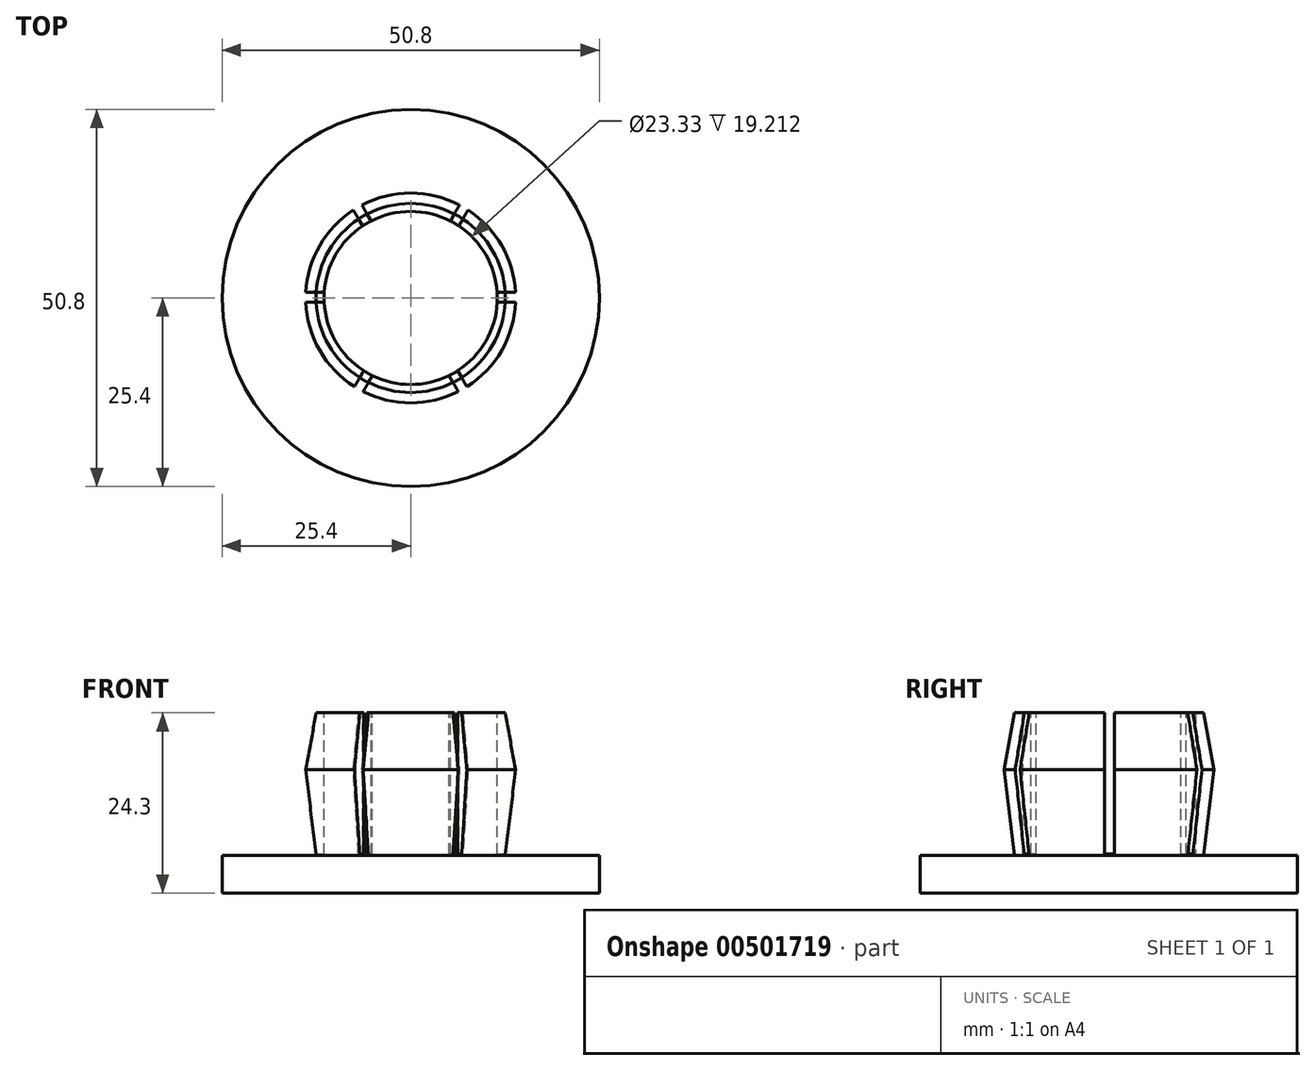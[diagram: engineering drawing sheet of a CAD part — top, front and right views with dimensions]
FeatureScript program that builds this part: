
annotation { "Feature Type Name" : "Feature", "Feature Type Description" : "" }
export const myFeature = defineFeature(function(context is Context, id is Id, definition is map)
    precondition{}
    {
        {
            var Q0;
            Q0=qCreatedBy(makeId("Top.planeOp"),FACE);
            var sketch = newSketch(context, id + "F0", { "sketchPlane" : qUnion([Q0])});
            skCircle(sketch, "E0", {"center": v(0, 0) * mm, "radius": 13.34 * mm});
            skCircle(sketch, "E1", {"center": v(0, 0) * mm, "radius": 25.4 * mm});
            skSolve(sketch);
        }
        {
            var Q0;
            Q0=makeQuery(id+"F0.imprint","IMPRINT",FACE,{"disambiguationData":[TD([[makeQuery(id+"F0.imprint","IMPRINT",EDGE,{"derivedFrom":sQuery(id+"F0.wireOp",EDGE,"E0")}),-1.0]])]});
            var Q1;
            Q1=makeQuery(id+"F0.imprint","IMPRINT",FACE,{"disambiguationData":[TD([[makeQuery(id+"F0.imprint","IMPRINT",EDGE,{"derivedFrom":sQuery(id+"F0.wireOp",EDGE,"E0")}),1.0]])]});
            extrude(context, id + "F1", {"entities" : qUnion([Q0, Q1]), "depth" : 5.08 * mm});
        }
        {
            var Q0;
            Q0=makeQuery(id+"F1.opExtrude","CAP_FACE",FACE,{"disambiguationData":[OSD([sQuery(id+"F0.wireOp",EDGE,"E1")])],"isStart":false});
            var sketch = newSketch(context, id + "F2", { "sketchPlane" : qUnion([Q0])});
            skCircle(sketch, "E2", {"center": v(0, 0) * mm, "radius": 13.34 * mm});
            skCircle(sketch, "E3", {"center": v(0, 0) * mm, "radius": 11.67 * mm});
            skSolve(sketch);
        }
        {
            var Q0;
            Q0=qCreatedBy(makeId("Right.planeOp"),FACE);
            var sketch = newSketch(context, id + "F3", { "sketchPlane" : qUnion([Q0])});
            skLineSegment(sketch, "E4", {"start": v(0, 5.08) * mm, "end": v(-12.74, 5.08) * mm});
            skLineSegment(sketch, "E5", {"start": v(-12.74, 5.08) * mm, "end": v(-14.14, 16.63) * mm});
            skLineSegment(sketch, "E6", {"start": v(-14.14, 16.63) * mm, "end": v(-12.74, 24.3) * mm});
            skLineSegment(sketch, "E7", {"start": v(-12.74, 24.3) * mm, "end": v(0, 24.3) * mm});
            skLineSegment(sketch, "E8", {"start": v(0, 24.3) * mm, "end": v(0, 5.08) * mm});
            skSolve(sketch);
        }
        {
            var Q0;
            Q0=makeQuery(id+"F3.imprint","IMPRINT",FACE,{"disambiguationData":[TD([[makeQuery(id+"F3.imprint","IMPRINT",EDGE,{"derivedFrom":sQuery(id+"F3.wireOp",EDGE,"E4")}),-1.0]])]});
            var Q1;
            Q1=sQuery(id+"F3.wireOp",EDGE,"E8");
            revolve(context, id + "F4", {"operationType" : NewBodyOperationType.ADD, "entities" : qUnion([Q0]), "axis" : qUnion([Q1]), "revolveType" : RevolveType.FULL});
        }
        {
            var Q0;
            Q0=makeQuery(id+"F2.imprint","IMPRINT",FACE,{"disambiguationData":[TD([[makeQuery(id+"F2.imprint","IMPRINT",EDGE,{"derivedFrom":sQuery(id+"F2.wireOp",EDGE,"E3")}),1.0]])]});
            extrude(context, id + "F5", {"entities" : qUnion([Q0]), "operationType" : NewBodyOperationType.REMOVE, "depth" : 25.4 * mm});
        }
        {
            var Q0;
            Q0=makeQuery(id+"F4.opRevolve","SWEPT_FACE",FACE,{"disambiguationData":[OSD([sQuery(id+"F3.wireOp",EDGE,"E7")])]});
            var sketch = newSketch(context, id + "F6", { "sketchPlane" : qUnion([Q0])});
            skLineSegment(sketch, "E9.bottom", {"start": v(-15.03, 0.76) * mm, "end": v(14.96, 0.76) * mm});
            skLineSegment(sketch, "E9.top", {"start": v(-15.03, -0.57) * mm, "end": v(14.96, -0.57) * mm});
            skLineSegment(sketch, "E9.left", {"start": v(-15.03, 0.76) * mm, "end": v(-15.03, -0.57) * mm});
            skLineSegment(sketch, "E9.right", {"start": v(14.96, 0.76) * mm, "end": v(14.96, -0.57) * mm});
            skLineSegment(sketch, "E10.1.0", {"start": v(6.85, -13.4) * mm, "end": v(8.01, -12.73) * mm});
            skLineSegment(sketch, "E10.1.1", {"start": v(6.85, -13.4) * mm, "end": v(-8.14, 12.57) * mm});
            skLineSegment(sketch, "E10.1.2", {"start": v(8.01, -12.73) * mm, "end": v(-6.98, 13.24) * mm});
            skLineSegment(sketch, "E10.1.3", {"start": v(-8.14, 12.57) * mm, "end": v(-6.98, 13.24) * mm});
            skLineSegment(sketch, "E10.2.0", {"start": v(8.18, 12.63) * mm, "end": v(7.02, 13.3) * mm});
            skLineSegment(sketch, "E10.2.1", {"start": v(8.18, 12.63) * mm, "end": v(-6.82, -13.34) * mm});
            skLineSegment(sketch, "E10.2.2", {"start": v(7.02, 13.3) * mm, "end": v(-7.98, -12.67) * mm});
            skLineSegment(sketch, "E10.2.3", {"start": v(-6.82, -13.34) * mm, "end": v(-7.98, -12.67) * mm});
            skPoint(sketch, "E10.center", {"position": v(0, 0) * mm});
            skSolve(sketch);
        }
        {
            var Q0;
            {var subQ0=sQuery(id+"F6.wireOp",EDGE,"E9.left");Q0=makeQuery(id+"F6.imprint","IMPRINT",FACE,{"disambiguationData":[TD([[makeQuery(id+"F6.imprint","IMPRINT",EDGE,{"derivedFrom":subQ0}),1.0]])]});}
            var Q1;
            {var subQ0=sQuery(id+"F6.wireOp",EDGE,"E9.bottom");var subQ1=sQuery(id+"F3.wireOp",EDGE,"E7");var subQ2=makeQuery(id+"F4.opRevolve","SWEPT_EDGE",EDGE,{"disambiguationData":[OSD([sQuery(id+"F3.wireOp",EDGE,"E6"),subQ1])]});var subQ3=makeQuery(id+"F6.imprint","INTERSECT",VERTEX,{"disambiguationData":[OD(0.0)],"derivedFrom":[subQ2,subQ0]});Q1=makeQuery(id+"F6.imprint","IMPRINT",FACE,{"disambiguationData":[TD([[makeQuery(id+"F6.imprint","IMPRINT",EDGE,{"disambiguationData":[TD([[subQ3,-1.0]])],"derivedFrom":subQ0}),-1.0]])]});}
            var Q2;
            {var subQ0=sQuery(id+"F6.wireOp",EDGE,"E10.1.3");Q2=makeQuery(id+"F6.imprint","IMPRINT",FACE,{"disambiguationData":[TD([[makeQuery(id+"F6.imprint","IMPRINT",EDGE,{"derivedFrom":subQ0}),-1.0]])]});}
            var Q3;
            {var subQ0=sQuery(id+"F6.wireOp",EDGE,"E10.1.1");var subQ1=sQuery(id+"F3.wireOp",EDGE,"E7");var subQ2=makeQuery(id+"F4.opRevolve","SWEPT_EDGE",EDGE,{"disambiguationData":[OSD([sQuery(id+"F3.wireOp",EDGE,"E6"),subQ1])]});var subQ3=makeQuery(id+"F6.imprint","INTERSECT",VERTEX,{"disambiguationData":[OD(1.0)],"derivedFrom":[subQ2,subQ0]});Q3=makeQuery(id+"F6.imprint","IMPRINT",FACE,{"disambiguationData":[TD([[makeQuery(id+"F6.imprint","IMPRINT",EDGE,{"disambiguationData":[TD([[subQ3,1.0]])],"derivedFrom":subQ0}),-1.0]])]});}
            var Q4;
            {var subQ0=sQuery(id+"F6.wireOp",EDGE,"E10.2.0");Q4=makeQuery(id+"F6.imprint","IMPRINT",FACE,{"disambiguationData":[TD([[makeQuery(id+"F6.imprint","IMPRINT",EDGE,{"derivedFrom":subQ0}),1.0]])]});}
            var Q5;
            {var subQ0=sQuery(id+"F6.wireOp",EDGE,"E10.2.1");var subQ1=sQuery(id+"F3.wireOp",EDGE,"E7");var subQ2=makeQuery(id+"F4.opRevolve","SWEPT_EDGE",EDGE,{"disambiguationData":[OSD([sQuery(id+"F3.wireOp",EDGE,"E6"),subQ1])]});var subQ3=makeQuery(id+"F6.imprint","INTERSECT",VERTEX,{"disambiguationData":[OD(0.0)],"derivedFrom":[subQ2,subQ0]});Q5=makeQuery(id+"F6.imprint","IMPRINT",FACE,{"disambiguationData":[TD([[makeQuery(id+"F6.imprint","IMPRINT",EDGE,{"disambiguationData":[TD([[subQ3,-1.0]])],"derivedFrom":subQ0}),-1.0]])]});}
            var Q6;
            {var subQ0=sQuery(id+"F6.wireOp",EDGE,"E9.bottom");var subQ1=sQuery(id+"F3.wireOp",EDGE,"E7");var subQ2=makeQuery(id+"F4.opRevolve","SWEPT_EDGE",EDGE,{"disambiguationData":[OSD([sQuery(id+"F3.wireOp",EDGE,"E6"),subQ1])]});var subQ3=makeQuery(id+"F6.imprint","INTERSECT",VERTEX,{"disambiguationData":[OD(1.0)],"derivedFrom":[subQ2,subQ0]});Q6=makeQuery(id+"F6.imprint","IMPRINT",FACE,{"disambiguationData":[TD([[makeQuery(id+"F6.imprint","IMPRINT",EDGE,{"disambiguationData":[TD([[subQ3,1.0]])],"derivedFrom":subQ0}),-1.0]])]});}
            var Q7;
            {var subQ0=sQuery(id+"F6.wireOp",EDGE,"E9.right");Q7=makeQuery(id+"F6.imprint","IMPRINT",FACE,{"disambiguationData":[TD([[makeQuery(id+"F6.imprint","IMPRINT",EDGE,{"derivedFrom":subQ0}),-1.0]])]});}
            var Q8;
            {var subQ0=sQuery(id+"F6.wireOp",EDGE,"E10.1.1");var subQ1=sQuery(id+"F3.wireOp",EDGE,"E7");var subQ2=makeQuery(id+"F4.opRevolve","SWEPT_EDGE",EDGE,{"disambiguationData":[OSD([sQuery(id+"F3.wireOp",EDGE,"E6"),subQ1])]});var subQ3=makeQuery(id+"F6.imprint","INTERSECT",VERTEX,{"disambiguationData":[OD(0.0)],"derivedFrom":[subQ2,subQ0]});Q8=makeQuery(id+"F6.imprint","IMPRINT",FACE,{"disambiguationData":[TD([[makeQuery(id+"F6.imprint","IMPRINT",EDGE,{"disambiguationData":[TD([[subQ3,-1.0]])],"derivedFrom":subQ0}),-1.0]])]});}
            var Q9;
            {var subQ0=sQuery(id+"F6.wireOp",EDGE,"E10.1.0");Q9=makeQuery(id+"F6.imprint","IMPRINT",FACE,{"disambiguationData":[TD([[makeQuery(id+"F6.imprint","IMPRINT",EDGE,{"derivedFrom":subQ0}),1.0]])]});}
            var Q10;
            {var subQ0=sQuery(id+"F6.wireOp",EDGE,"E10.2.1");var subQ1=sQuery(id+"F3.wireOp",EDGE,"E7");var subQ2=makeQuery(id+"F4.opRevolve","SWEPT_EDGE",EDGE,{"disambiguationData":[OSD([sQuery(id+"F3.wireOp",EDGE,"E6"),subQ1])]});var subQ3=makeQuery(id+"F6.imprint","INTERSECT",VERTEX,{"disambiguationData":[OD(1.0)],"derivedFrom":[subQ2,subQ0]});Q10=makeQuery(id+"F6.imprint","IMPRINT",FACE,{"disambiguationData":[TD([[makeQuery(id+"F6.imprint","IMPRINT",EDGE,{"disambiguationData":[TD([[subQ3,1.0]])],"derivedFrom":subQ0}),-1.0]])]});}
            var Q11;
            {var subQ0=sQuery(id+"F6.wireOp",EDGE,"E10.2.3");Q11=makeQuery(id+"F6.imprint","IMPRINT",FACE,{"disambiguationData":[TD([[makeQuery(id+"F6.imprint","IMPRINT",EDGE,{"derivedFrom":subQ0}),-1.0]])]});}
            extrude(context, id + "F7", {"entities" : qUnion([Q0, Q1, Q2, Q3, Q4, Q5, Q6, Q7, Q8, Q9, Q10, Q11]), "operationType" : NewBodyOperationType.REMOVE, "oppositeDirection" : true, "depth" : 19.05 * mm});
        }
    });
